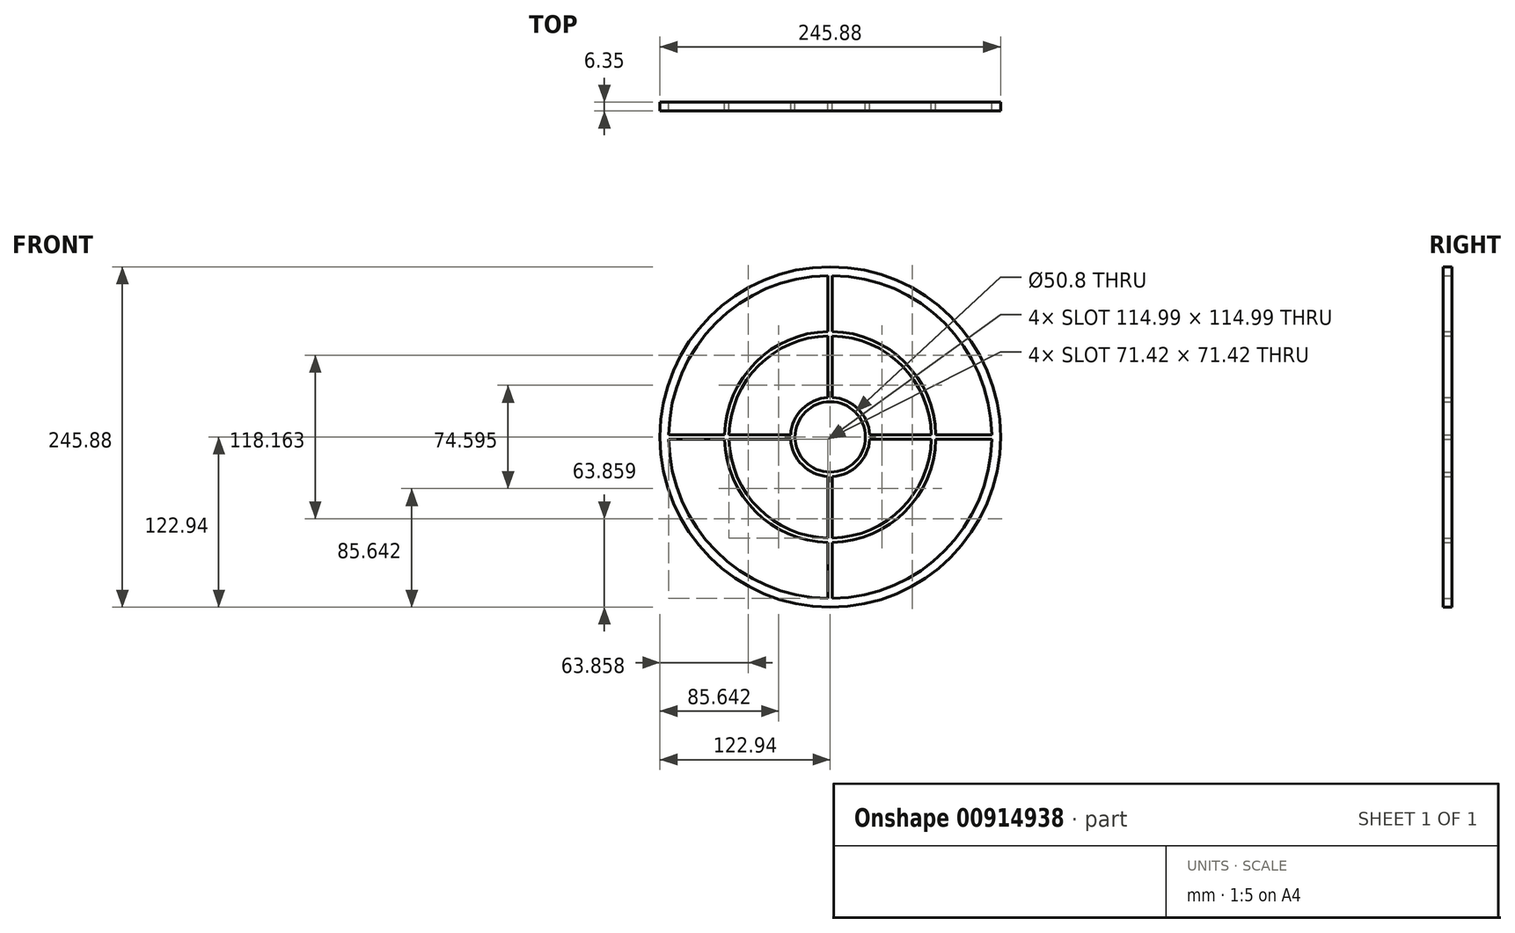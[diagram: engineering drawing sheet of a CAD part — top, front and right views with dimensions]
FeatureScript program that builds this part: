
annotation { "Feature Type Name" : "Feature", "Feature Type Description" : "" }
export const myFeature = defineFeature(function(context is Context, id is Id, definition is map)
    precondition{}
    {
        {
            var Q0;
            Q0=qCreatedBy(makeId("Front.planeOp"),FACE);
            var sketch = newSketch(context, id + "F0", { "sketchPlane" : qUnion([Q0])});
            skCircle(sketch, "E0", {"center": v(0, 0) * mm, "radius": 122.94 * mm});
            skArc(sketch, "E1.0", {"start": v(-116.58, -1.6) * mm, "mid": v(-82.44, -82.44) * mm, "end": v(-1.59, -116.58) * mm});
            skArc(sketch, "E2", {"start": v(-76.18, -1.59) * mm, "mid": v(-53.88, -53.88) * mm, "end": v(-1.59, -76.18) * mm});
            skArc(sketch, "E3.0", {"start": v(-73, -1.59) * mm, "mid": v(-51.64, -51.64) * mm, "end": v(-1.59, -73) * mm});
            skCircle(sketch, "E4", {"center": v(0, 0) * mm, "radius": 25.4 * mm});
            skArc(sketch, "E5.0", {"start": v(-28.53, -1.59) * mm, "mid": v(-20.2, -20.2) * mm, "end": v(-1.59, -28.53) * mm});
            skLineSegment(sketch, "E6.left", {"start": v(1.59, -116.58) * mm, "end": v(1.59, -76.18) * mm});
            skLineSegment(sketch, "E6.right", {"start": v(-1.59, -116.58) * mm, "end": v(-1.59, -76.18) * mm});
            skLineSegment(sketch, "E7.trimOffspring", {"start": v(-76.18, 1.59) * mm, "end": v(-116.58, 1.6) * mm});
            skLineSegment(sketch, "E8.trimOffspring", {"start": v(-76.18, -1.59) * mm, "end": v(-116.58, -1.6) * mm});
            skLineSegment(sketch, "E9.trimOffspring", {"start": v(-28.53, 1.59) * mm, "end": v(-73, 1.59) * mm});
            skLineSegment(sketch, "E10.trimOffspring", {"start": v(-28.53, -1.59) * mm, "end": v(-73, -1.59) * mm});
            skLineSegment(sketch, "E11.trimOffspring", {"start": v(-1.59, 28.53) * mm, "end": v(-1.59, 73) * mm});
            skLineSegment(sketch, "E12.trimOffspring", {"start": v(1.59, 28.53) * mm, "end": v(1.59, 73) * mm});
            skPoint(sketch, "E13.end.orphan", {"position": v(1.59, 0) * mm});
            skArc(sketch, "E14.trimOffspring", {"start": v(28.53, 1.59) * mm, "mid": v(20.2, 20.2) * mm, "end": v(1.59, 28.53) * mm});
            skArc(sketch, "E15.trimOffspring", {"start": v(1.59, -28.53) * mm, "mid": v(20.2, -20.2) * mm, "end": v(28.53, -1.59) * mm});
            skArc(sketch, "E16.trimOffspring", {"start": v(-1.59, 28.53) * mm, "mid": v(-20.2, 20.2) * mm, "end": v(-28.53, 1.59) * mm});
            skPoint(sketch, "E17.orphan", {"position": v(0, 28.58) * mm});
            skArc(sketch, "E18.trimOffspring", {"start": v(73, 1.59) * mm, "mid": v(51.64, 51.64) * mm, "end": v(1.59, 73) * mm});
            skLineSegment(sketch, "E19.trimOffspring", {"start": v(73, 1.59) * mm, "end": v(28.53, 1.59) * mm});
            skLineSegment(sketch, "E20.trimOffspring", {"start": v(73, -1.59) * mm, "end": v(28.53, -1.59) * mm});
            skArc(sketch, "E21.trimOffspring", {"start": v(76.18, 1.59) * mm, "mid": v(53.88, 53.88) * mm, "end": v(1.59, 76.18) * mm});
            skArc(sketch, "E22.trimOffspring", {"start": v(116.58, 1.6) * mm, "mid": v(82.44, 82.44) * mm, "end": v(1.59, 116.58) * mm});
            skLineSegment(sketch, "E23.trimOffspring", {"start": v(116.58, 1.6) * mm, "end": v(76.18, 1.59) * mm});
            skLineSegment(sketch, "E24.trimOffspring", {"start": v(116.58, -1.6) * mm, "end": v(76.18, -1.59) * mm});
            skPoint(sketch, "E25.start.orphan", {"position": v(126.67, 0) * mm});
            skPoint(sketch, "E26.orphan", {"position": v(1.59, -128.77) * mm});
            skArc(sketch, "E27.trimOffspring", {"start": v(1.59, -116.58) * mm, "mid": v(82.44, -82.44) * mm, "end": v(116.58, -1.6) * mm});
            skArc(sketch, "E28.trimOffspring", {"start": v(1.59, -76.18) * mm, "mid": v(53.88, -53.88) * mm, "end": v(76.18, -1.59) * mm});
            skArc(sketch, "E29.trimOffspring", {"start": v(1.59, -73) * mm, "mid": v(51.64, -51.64) * mm, "end": v(73, -1.59) * mm});
            skLineSegment(sketch, "E30.trimOffspring", {"start": v(1.59, -73) * mm, "end": v(1.59, -28.53) * mm});
            skLineSegment(sketch, "E31.trimOffspring", {"start": v(-1.59, -73) * mm, "end": v(-1.59, -28.53) * mm});
            skArc(sketch, "E32.trimOffspring", {"start": v(-1.59, 116.58) * mm, "mid": v(-82.44, 82.44) * mm, "end": v(-116.58, 1.6) * mm});
            skArc(sketch, "E33.trimOffspring", {"start": v(-1.59, 76.18) * mm, "mid": v(-53.88, 53.88) * mm, "end": v(-76.18, 1.59) * mm});
            skLineSegment(sketch, "E34.trimOffspring", {"start": v(-1.59, 76.18) * mm, "end": v(-1.59, 116.58) * mm});
            skLineSegment(sketch, "E35.trimOffspring", {"start": v(1.59, 76.18) * mm, "end": v(1.59, 116.58) * mm});
            skArc(sketch, "E36.trimOffspring", {"start": v(-1.59, 73) * mm, "mid": v(-51.64, 51.64) * mm, "end": v(-73, 1.59) * mm});
            skSolve(sketch);
        }
        {
            var Q0;
            Q0 = qSketchRegion(id + "F0", true);
            extrude(context, id + "F1", {"entities" : qUnion([Q0]), "depth" : 6.35 * mm, "offsetDistance" : 25.4 * mm});
        }
    });
